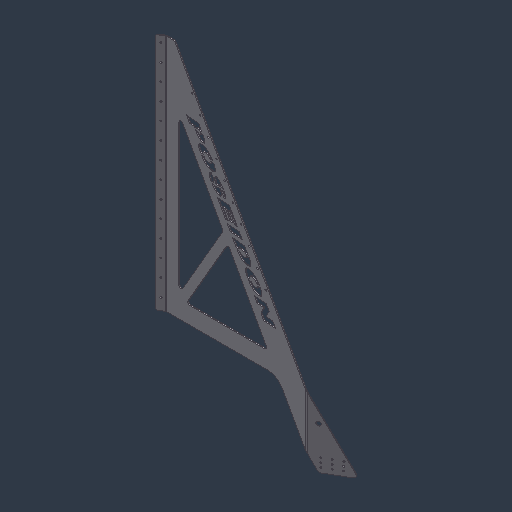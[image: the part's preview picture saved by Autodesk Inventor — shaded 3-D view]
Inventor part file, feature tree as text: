
AUTODESK INVENTOR PART (.ipt)
format: ipt  version: 2024.3 (Build 283343000, 343)  size: 685,056 bytes
history: native  units: mm (DEFAULTED — no unit token found)
features: other x5, plane x2, hole x2, boolean_combine x2, sketch x2, pattern_linear x1
ambient origin geometry x8: Origin, YZ Plane, XZ Plane, XY Plane, X Axis, Y Axis, Z Axis, Center Point
bodies: Solid7 (feature_tree), Solid8 (feature_tree)
feature tree (14):
  other  "PLATE,SIDE,BRACE,ELEVATOR.ipt"
  plane  "Work Plane6"
  hole  "Hole2"  [1 undecoded]
  pattern_linear  "Rectangular Pattern1"  Spacing1=20.594885mm  [1 undecoded]
  boolean_combine  "Combine6"
  boolean_combine  "Combine7"
  hole  "Hole3"  [1 undecoded]
  other  "Solid2::PLATE,SIDE,BRACE,ELEVATOR.ipt"
  other  "TaggingFeature1"
  plane  "Work Plane5"
  sketch  "Sketch6"  dims[d88=10.0mm d89=3.048mm]
  other  "Solid7::PLATE,SIDE,BRACE,ELEVATOR.ipt"
  other  "Solid8::PLATE,SIDE,BRACE,ELEVATOR.ipt"
  sketch  "Sketch7"  dims[d95=-334.9625mm d99=4.9784mm d100=19.05mm d101=9.779mm d102=1.9558mm d103=14.3117mm d104=3.175mm d105=20.594885mm d106=100.0mm d108=50.8mm d109=7.937425mm d110=117.689036mm d113=3.048mm d114=3.048mm d115=127.0mm d116=25.4mm d117=12.7508mm d118=19.05mm d119=9.525mm d120=6.35mm d121=14.3117mm d122=3.175mm d123=20.594885mm]
note: 3 required parameter values undecoded (feature->parameter linkage not recoverable at this tier; creation-order binding heuristic only, values carry confidence <= 0.55)
